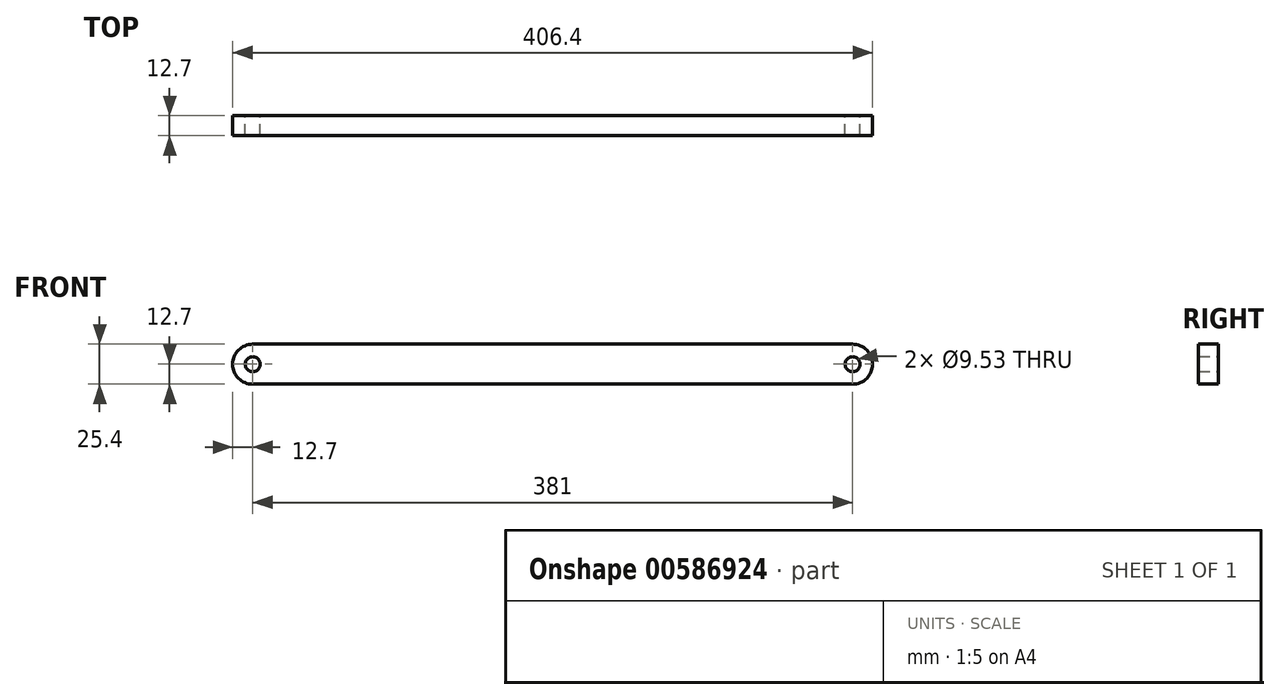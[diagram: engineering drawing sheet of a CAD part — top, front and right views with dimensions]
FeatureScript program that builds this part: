
annotation { "Feature Type Name" : "Feature", "Feature Type Description" : "" }
export const myFeature = defineFeature(function(context is Context, id is Id, definition is map)
    precondition{}
    {
        {
            var Q0;
            Q0=qCreatedBy(makeId("Front.planeOp"),FACE);
            var sketch = newSketch(context, id + "F0", { "sketchPlane" : qUnion([Q0])});
            skCircle(sketch, "E0", {"center": v(0, 0) * mm, "radius": 4.76 * mm});
            skArc(sketch, "E1", {"start": v(0, 12.7) * mm, "mid": v(-12.7, 0) * mm, "end": v(0, -12.7) * mm});
            skCircle(sketch, "E2", {"center": v(381, 0) * mm, "radius": 4.76 * mm});
            skArc(sketch, "E3", {"start": v(381, -12.7) * mm, "mid": v(393.7, 0) * mm, "end": v(381, 12.7) * mm});
            skLineSegment(sketch, "E4", {"start": v(0, 12.7) * mm, "end": v(381, 12.7) * mm});
            skLineSegment(sketch, "E5", {"start": v(0, -12.7) * mm, "end": v(381, -12.7) * mm});
            skSolve(sketch);
        }
        {
            var Q0;
            Q0=makeQuery(id+"F0.imprint","IMPRINT",FACE,{"disambiguationData":[TD([[makeQuery(id+"F0.imprint","IMPRINT",EDGE,{"derivedFrom":sQuery(id+"F0.wireOp",EDGE,"E0")}),-1.0]])]});
            extrude(context, id + "F1", {"entities" : qUnion([Q0]), "depth" : 12.7 * mm, "offsetDistance" : 25.4 * mm});
        }
    });
